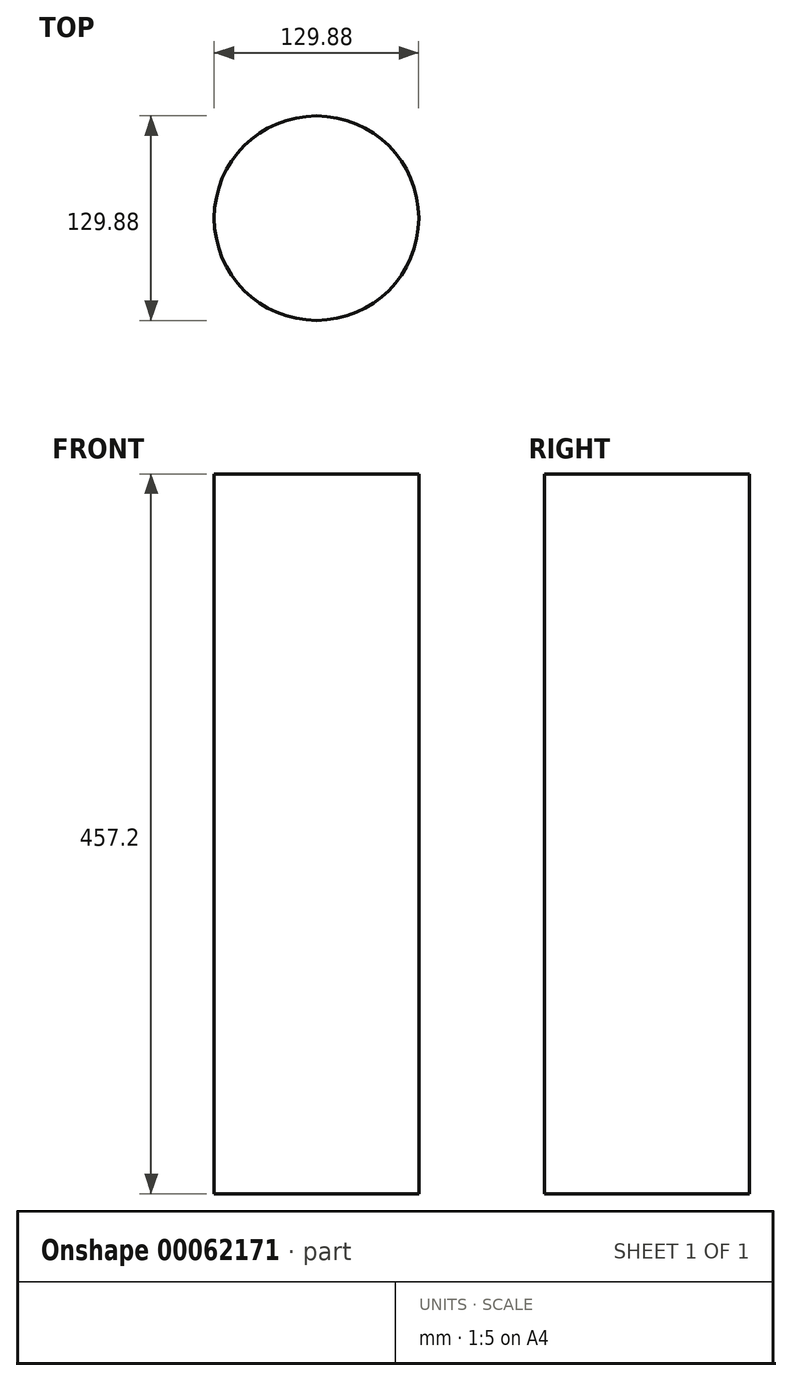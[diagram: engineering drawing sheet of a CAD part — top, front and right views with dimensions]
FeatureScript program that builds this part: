
annotation { "Feature Type Name" : "Feature", "Feature Type Description" : "" }
export const myFeature = defineFeature(function(context is Context, id is Id, definition is map)
    precondition{}
    {
        {
            var Q0;
            Q0=qCreatedBy(makeId("Top.planeOp"),FACE);
            var sketch = newSketch(context, id + "F0", { "sketchPlane" : qUnion([Q0])});
            skCircle(sketch, "E0", {"center": v(0, 0) * mm, "radius": 64.94 * mm});
            skSolve(sketch);
        }
        {
            var Q0;
            Q0 = qSketchRegion(id + "F0", true);
            extrude(context, id + "F1", {"entities" : qUnion([Q0]), "endBound" : BoundingType.SYMMETRIC, "depth" : 457.2 * mm});
        }
    });
